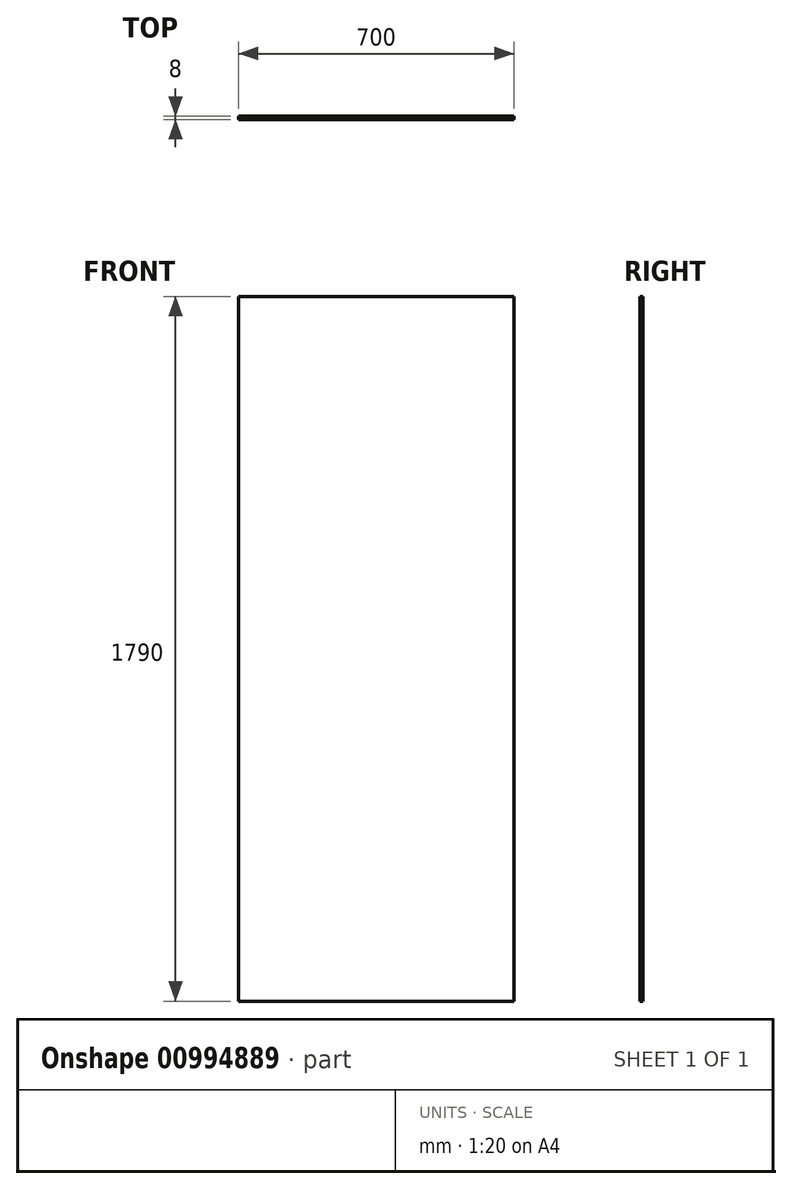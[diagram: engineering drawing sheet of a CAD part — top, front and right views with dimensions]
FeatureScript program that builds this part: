
annotation { "Feature Type Name" : "Feature", "Feature Type Description" : "" }
export const myFeature = defineFeature(function(context is Context, id is Id, definition is map)
    precondition{}
    {
        {
            var Q0;
            Q0=qCreatedBy(makeId("Front.planeOp"), FACE);
            var sketch = newSketch(context, id + "F0", { "sketchPlane" : qUnion([Q0])});
            skLineSegment(sketch, "E0.bottom", {"start": v(0, 0) * mm, "end": v(700, 0) * mm});
            skLineSegment(sketch, "E0.top", {"start": v(0, 1790) * mm, "end": v(700, 1790) * mm});
            skLineSegment(sketch, "E0.left", {"start": v(0, 0) * mm, "end": v(0, 1790) * mm});
            skLineSegment(sketch, "E0.right", {"start": v(700, 0) * mm, "end": v(700, 1790) * mm});
            skSolve(sketch);
        }
        {
            var Q0;
            Q0 = qSketchRegion(id + "F0", true);
            extrude(context, id + "F1", {"entities" : qUnion([Q0]), "depth" : 8 * mm, "offsetDistance" : 25 * mm});
        }
    });
